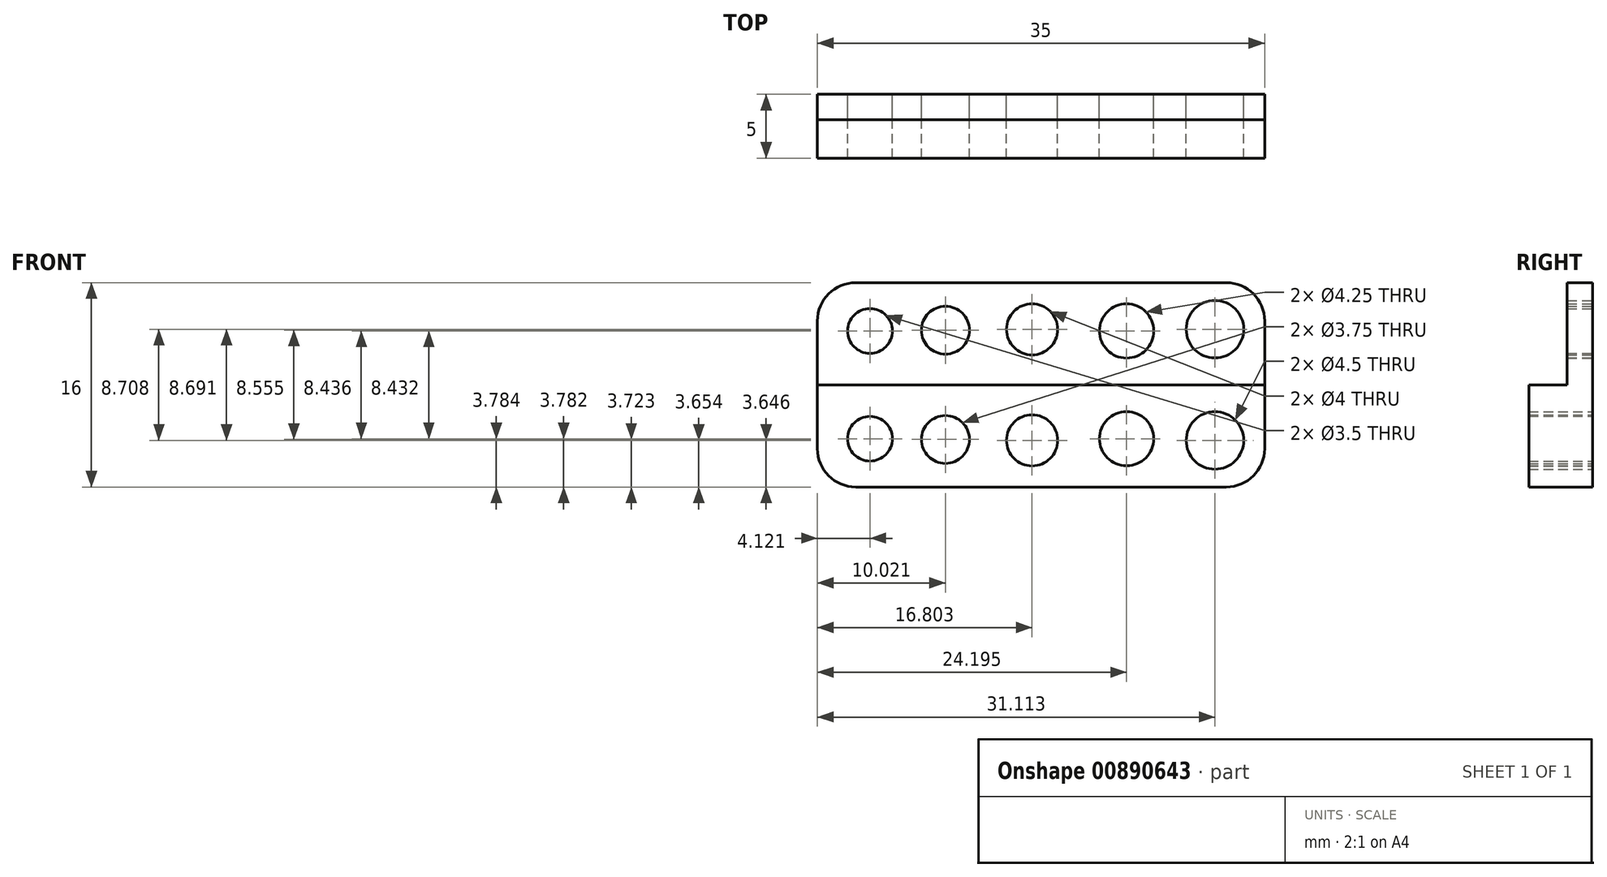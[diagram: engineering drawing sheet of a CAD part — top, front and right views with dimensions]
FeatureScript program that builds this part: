
annotation { "Feature Type Name" : "Feature", "Feature Type Description" : "" }
export const myFeature = defineFeature(function(context is Context, id is Id, definition is map)
    precondition{}
    {
        {
            var Q0;
            Q0=qCreatedBy(makeId("Front.planeOp"),FACE);
            var sketch = newSketch(context, id + "F0", { "sketchPlane" : qUnion([Q0])});
            skLineSegment(sketch, "E0.bottom", {"start": v(0, 0) * mm, "end": v(35, 0) * mm});
            skLineSegment(sketch, "E0.top", {"start": v(0, -8) * mm, "end": v(35, -8) * mm});
            skLineSegment(sketch, "E0.left", {"start": v(0, 0) * mm, "end": v(0, -8) * mm});
            skLineSegment(sketch, "E0.right", {"start": v(35, 0) * mm, "end": v(35, -8) * mm});
            skCircle(sketch, "E1", {"center": v(4.12, -3.78) * mm, "radius": 1.75 * mm});
            skCircle(sketch, "E2", {"center": v(16.8, -3.65) * mm, "radius": 2 * mm});
            skCircle(sketch, "E3", {"center": v(31.11, -3.65) * mm, "radius": 2.25 * mm});
            skCircle(sketch, "E4", {"center": v(10.02, -3.72) * mm, "radius": 1.88 * mm});
            skCircle(sketch, "E5", {"center": v(24.2, -3.78) * mm, "radius": 2.12 * mm});
            skLineSegment(sketch, "E6.MirrorCS", {"start": v(0, -16) * mm, "end": v(35, -16) * mm});
            skCircle(sketch, "E7.MirrorC", {"center": v(16.8, -12.35) * mm, "radius": 2 * mm});
            skCircle(sketch, "E8.MirrorC", {"center": v(4.12, -12.22) * mm, "radius": 1.75 * mm});
            skLineSegment(sketch, "E9.MirrorCS", {"start": v(0, -16) * mm, "end": v(0, -8) * mm});
            skLineSegment(sketch, "E10.MirrorCS", {"start": v(35, -16) * mm, "end": v(35, -8) * mm});
            skCircle(sketch, "E11.MirrorC", {"center": v(31.11, -12.35) * mm, "radius": 2.25 * mm});
            skCircle(sketch, "E12.MirrorC", {"center": v(10.02, -12.28) * mm, "radius": 1.88 * mm});
            skCircle(sketch, "E13.MirrorC", {"center": v(24.2, -12.22) * mm, "radius": 2.12 * mm});
            skSolve(sketch);
        }
        {
            var Q0;
            Q0=makeQuery(id+"F0.imprint","IMPRINT",FACE,{"disambiguationData":[TD([[makeQuery(id+"F0.imprint","IMPRINT",EDGE,{"derivedFrom":sQuery(id+"F0.wireOp",EDGE,"E0.bottom")}),-1.0]])]});
            extrude(context, id + "F1", {"entities" : qUnion([Q0]), "depth" : 2 * mm, "offsetDistance" : 25 * mm});
        }
        {
            var Q0;
            Q0=makeQuery(id+"F0.imprint","IMPRINT",FACE,{"disambiguationData":[TD([[makeQuery(id+"F0.imprint","IMPRINT",EDGE,{"derivedFrom":sQuery(id+"F0.wireOp",EDGE,"E0.top")}),-1.0]])]});
            extrude(context, id + "F2", {"entities" : qUnion([Q0]), "operationType" : NewBodyOperationType.ADD, "depth" : 2 * mm, "offsetDistance" : 25 * mm});
        }
        {
            var Q0;
            Q0=makeQuery(id+"F0.imprint","IMPRINT",FACE,{"disambiguationData":[TD([[makeQuery(id+"F0.imprint","IMPRINT",EDGE,{"derivedFrom":sQuery(id+"F0.wireOp",EDGE,"E11.MirrorC")}),-1.0]])]});
            var Q1;
            Q1=makeQuery(id+"F0.imprint","IMPRINT",FACE,{"disambiguationData":[TD([[makeQuery(id+"F0.imprint","IMPRINT",EDGE,{"derivedFrom":sQuery(id+"F0.wireOp",EDGE,"E13.MirrorC")}),-1.0]])]});
            var Q2;
            Q2=makeQuery(id+"F0.imprint","IMPRINT",FACE,{"disambiguationData":[TD([[makeQuery(id+"F0.imprint","IMPRINT",EDGE,{"derivedFrom":sQuery(id+"F0.wireOp",EDGE,"E7.MirrorC")}),-1.0]])]});
            var Q3;
            Q3=makeQuery(id+"F0.imprint","IMPRINT",FACE,{"disambiguationData":[TD([[makeQuery(id+"F0.imprint","IMPRINT",EDGE,{"derivedFrom":sQuery(id+"F0.wireOp",EDGE,"E12.MirrorC")}),-1.0]])]});
            var Q4;
            Q4=makeQuery(id+"F0.imprint","IMPRINT",FACE,{"disambiguationData":[TD([[makeQuery(id+"F0.imprint","IMPRINT",EDGE,{"derivedFrom":sQuery(id+"F0.wireOp",EDGE,"E8.MirrorC")}),-1.0]])]});
            var Q5;
            Q5=sQuery(id+"F0.wireOp",EDGE,"E8.MirrorC");
            var Q6;
            Q6=sQuery(id+"F0.wireOp",EDGE,"E12.MirrorC");
            var Q7;
            Q7=sQuery(id+"F0.wireOp",EDGE,"E7.MirrorC");
            var Q8;
            Q8=sQuery(id+"F0.wireOp",EDGE,"E13.MirrorC");
            var Q9;
            Q9=sQuery(id+"F0.wireOp",EDGE,"E11.MirrorC");
            extrude(context, id + "F3", {"entities" : qUnion([Q0, Q1, Q2, Q3, Q4]), "operationType" : NewBodyOperationType.ADD, "surfaceEntities" : qUnion([Q5, Q6, Q7, Q8, Q9]), "depth" : 5 * mm, "offsetDistance" : 25 * mm});
        }
        {
            var Q0;
            Q0=makeQuery(id+"F1.opExtrude","SWEPT_EDGE",EDGE,{"disambiguationData":[OSD([sQuery(id+"F0.wireOp",EDGE,"E0.bottom"),sQuery(id+"F0.wireOp",EDGE,"E0.left")])]});
            var Q1;
            Q1=makeQuery(id+"F2.opExtrude","SWEPT_EDGE",EDGE,{"disambiguationData":[OSD([sQuery(id+"F0.wireOp",EDGE,"E6.MirrorCS"),sQuery(id+"F0.wireOp",EDGE,"E9.MirrorCS")])]});
            var Q2;
            Q2=makeQuery(id+"F2.opExtrude","SWEPT_EDGE",EDGE,{"disambiguationData":[OSD([sQuery(id+"F0.wireOp",EDGE,"E6.MirrorCS"),sQuery(id+"F0.wireOp",EDGE,"E10.MirrorCS")])]});
            var Q3;
            Q3=makeQuery(id+"F1.opExtrude","SWEPT_EDGE",EDGE,{"disambiguationData":[OSD([sQuery(id+"F0.wireOp",EDGE,"E0.bottom"),sQuery(id+"F0.wireOp",EDGE,"E0.right")])]});
            fillet(context, id + "F4", {"entities" : qUnion([Q0, Q1, Q2, Q3]), "radius" : 3 * mm, "tangentPropagation" : true, "allowEdgeOverflow" : false});
        }
    });
